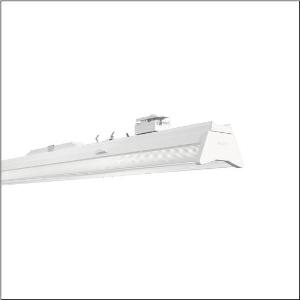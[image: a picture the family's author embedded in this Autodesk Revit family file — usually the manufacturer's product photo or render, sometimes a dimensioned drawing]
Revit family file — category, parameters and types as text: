
# Revit family: licross_r__21_performance_mo_52td16mn4a5g_2767
name_source: partatom
category: Lighting Fixtures
units: mm (PartAtom-declared; Revit-internal decimal feet)

## family parameters
Cut with Voids When Loaded = No
Host = Face
Light Source = No
Part Type = Normal
Room Calculation Point = No
Round Connector Dimension = Use Diameter
Shared = No

## types (1)
- --- (1 x LED, 10890 lm, 60.5 W, 4000K)
    Apparent Load = 61 VA
    CIE Flux Codes = 66 88 96 79 100
    Color Rendering = 80
    Color Temperature = 4000K
    Default Elevation = 1800 mm
    Description = Licross® 21 Performance MO, luminaire insert, of sheet steel, galvanised, coil coated, white, length: 1.500mm, width: 120mm, height: 123mm, LED rated luminous flux: 10.890lm, light colour: 840, control gear: ON/OFF Multilumen, with plug, 3-pole, with phase selection, mains connection: 220..240V, AC, 50/60Hz, rated input power: 61W, halogen-free wiring, primary light control with lens, of plastic, primary optical cover: cover, of PMMA, light emission: direct/indirect distribution, primary light characteristic: symmetric, protection rating (complete): IP54, insulation class (complete): insulation class I (protective earthing), certification: CE, ENEC, UKCA, protection symbol: D if used in an environment with non-conductive dust loads with corresponding accessories, impact resistance: IK06, permissible ambient temperature for indoor applications: -35..+45°C, corresponds to IFS (International Featured Standards) requirements for safety and quality in the food industry, reducing of maximum allowable ambient temperature of 5°C with ceiling mounting, LABS conformity tested according to VDMA 24364:2018-05, packaging unit: 1 piece
    Height = 114 mm
    Lamp = 1 x LED
    Lamp Light Flux = 10890 lm
    Lamp Power = 60.5 W
    Lamp count = 1
    Length = 1500 mm
    Luminous efficacy = 180 lm/W
    Manufacturer = Siteco
    ModVariant = No
    Model = 52TD16MN4A5G
    Mounting Place = Ceiling
    Mounting Type = Pendant
    Number of Poles = 1
    OnlyDefault = Yes
    Power Factor = 1
    Product Name = Licross® 21 Performance MO
    Product group = luminaire insert
    ProductGroupID = 901
    Protection Class = Protection class I
    Protection Degree = IP 54
    RLX_Detail_Level = 1
    RLX_Emergency_Light_Flux = 0 lm
    RLX_Emergency_Type = 0
    RLX_Emergency_Type_DB = No
    RlxData = <blob elided: 31829 chars, md5=0b3dfddf>
    Socket = socket
    Standby Power = 0 W
    System Light Flux = 10890 lm
    System Power = 61 W
    Type Comments = factory setting: luminous flux: 100 % | (A | C | E) | 140 mA
    Type Image = l_1256138.jpg
    URL = http://relux.com
    VarID = @adj_078071
    Voltage = 0 V
    Weight = 0.00 kg
    Width = 120 mm

## geometry (parser evidence)
native form markers: Blend x4, Sweep x12
no freeform markers — native parametric forms only
